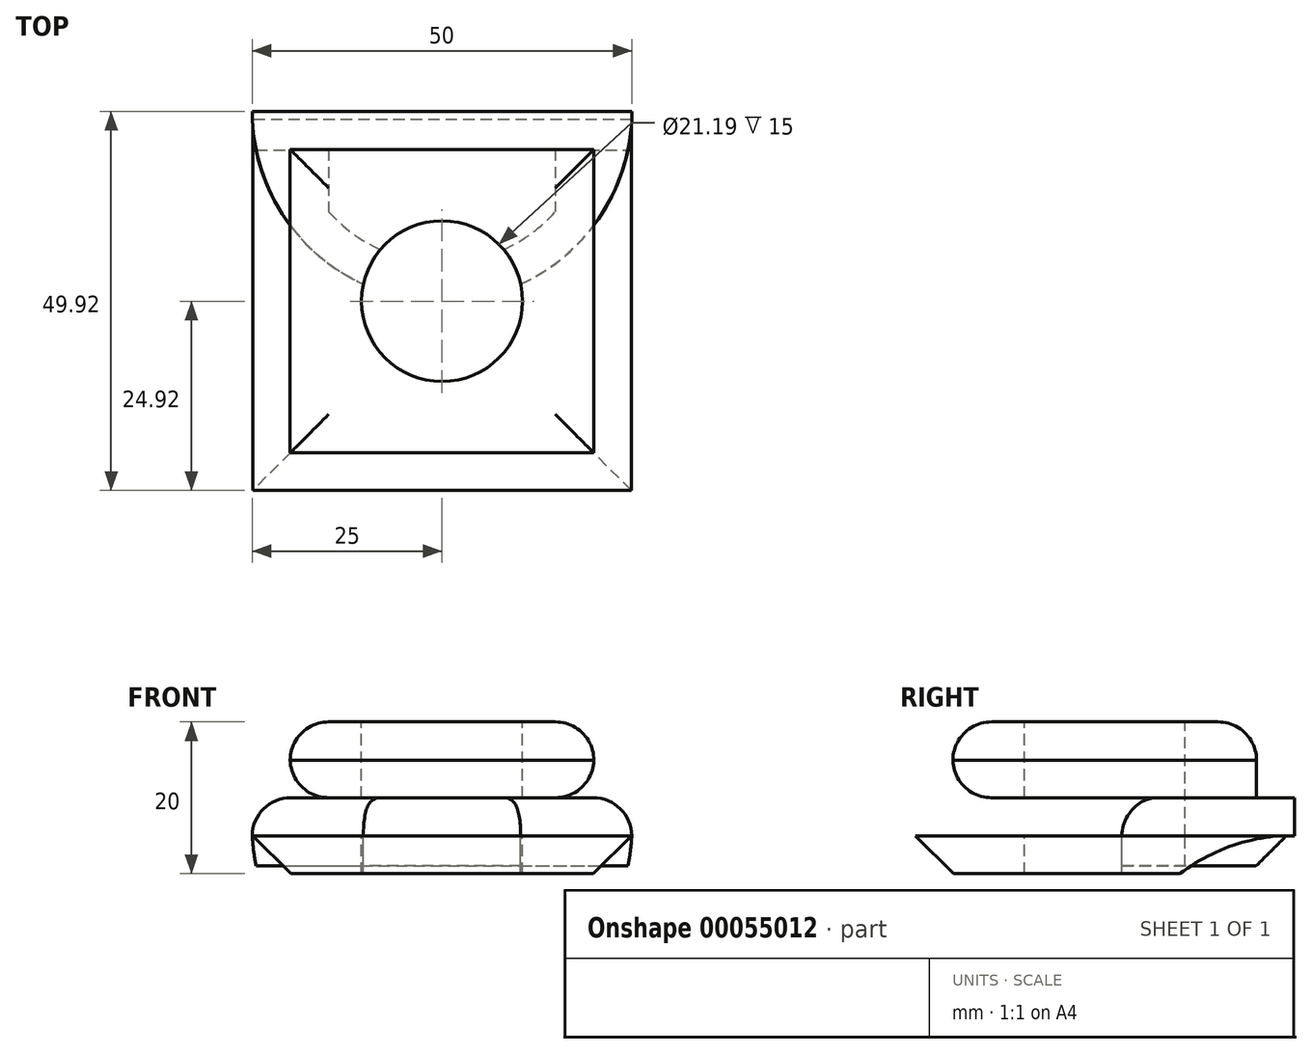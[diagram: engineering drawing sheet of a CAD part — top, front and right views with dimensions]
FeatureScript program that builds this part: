
annotation { "Feature Type Name" : "Feature", "Feature Type Description" : "" }
export const myFeature = defineFeature(function(context is Context, id is Id, definition is map)
    precondition{}
    {
        {
            var Q0;
            Q0=qCreatedBy(makeId("Top.planeOp"),FACE);
            var sketch = newSketch(context, id + "F0", { "sketchPlane" : qUnion([Q0])});
            skLineSegment(sketch, "E0.rect.bottom", {"start": v(25, -25) * mm, "end": v(-25, -25) * mm});
            skLineSegment(sketch, "E0.rect.top", {"start": v(25, 25) * mm, "end": v(-25, 25) * mm});
            skLineSegment(sketch, "E0.rect.left", {"start": v(25, -25) * mm, "end": v(25, 25) * mm});
            skLineSegment(sketch, "E0.rect.right", {"start": v(-25, -25) * mm, "end": v(-25, 25) * mm});
            skPoint(sketch, "E0.rect.middle", {"position": v(0, 0) * mm});
            skArc(sketch, "E1", {"start": v(-25, 25) * mm, "mid": v(0, 0) * mm, "end": v(25, 25) * mm});
            skSolve(sketch);
        }
        {
            var Q0;
            Q0=makeQuery(id+"F0.imprint","IMPRINT",FACE,{"disambiguationData":[TD([[makeQuery(id+"F0.imprint","IMPRINT",EDGE,{"derivedFrom":sQuery(id+"F0.wireOp",EDGE,"E0.rect.bottom")}),-1.0]])]});
            extrude(context, id + "F1", {"entities" : qUnion([Q0]), "oppositeDirection" : true, "depth" : 5 * mm});
        }
        {
            var Q0;
            Q0=makeQuery(id+"F0.imprint","IMPRINT",FACE,{"disambiguationData":[TD([[makeQuery(id+"F0.imprint","IMPRINT",EDGE,{"derivedFrom":sQuery(id+"F0.wireOp",EDGE,"E0.rect.top")}),1.0]])]});
            extrude(context, id + "F2", {"entities" : qUnion([Q0]), "operationType" : NewBodyOperationType.ADD, "depth" : 5 * mm});
        }
        {
            var Q0;
            Q0=makeQuery(id+"F2.opExtrude","CAP_EDGE",EDGE,{"disambiguationData":[OSD([sQuery(id+"F0.wireOp",EDGE,"E1")])],"isStart":false});
            fillet(context, id + "F3", {"entities" : qUnion([Q0]), "radius" : 5.08 * mm, "tangentPropagation" : true, "allowEdgeOverflow" : false});
        }
        {
            var Q0;
            Q0=makeQuery(id+"F2.opExtrude","CAP_FACE",FACE,{"disambiguationData":[OSD([sQuery(id+"F0.wireOp",EDGE,"E0.rect.top"),sQuery(id+"F0.wireOp",EDGE,"E1")])],"isStart":true});
            extrude(context, id + "F4", {"entities" : qUnion([Q0]), "depth" : 4 * mm});
        }
        {
            var Q0;
            Q0=makeQuery(id+"F1.opExtrude","CAP_EDGE",EDGE,{"disambiguationData":[OSD([sQuery(id+"F0.wireOp",EDGE,"E0.rect.right")])],"isStart":false});
            var Q1;
            Q1=makeQuery(id+"F1.opExtrude","CAP_EDGE",EDGE,{"disambiguationData":[OSD([sQuery(id+"F0.wireOp",EDGE,"E0.rect.bottom")])],"isStart":false});
            var Q2;
            Q2=makeQuery(id+"F1.opExtrude","CAP_EDGE",EDGE,{"disambiguationData":[OSD([sQuery(id+"F0.wireOp",EDGE,"E0.rect.left")])],"isStart":false});
            var Q3;
            Q3=makeQuery(id+"F4.opExtrude","CAP_EDGE",EDGE,{"disambiguationData":[OSD([sQuery(id+"F0.wireOp",EDGE,"E0.rect.top")])],"isStart":false});
            chamfer(context, id + "F5", {"entities" : qUnion([Q0, Q1, Q2, Q3]), "width" : 5.08 * mm, "tangentPropagation" : true});
        }
        {
            var Q0;
            Q0=makeQuery(id+"F2.opExtrude","CAP_FACE",FACE,{"disambiguationData":[OSD([sQuery(id+"F0.wireOp",EDGE,"E0.rect.top"),sQuery(id+"F0.wireOp",EDGE,"E1")])],"isStart":false});
            cPlane(context, id + "F6", {"entities" : qUnion([Q0]), "cplaneType" : CPlaneType.OFFSET, "offset" : 0 * mm, "width" : 152.4 * mm, "height" : 152.4 * mm});
        }
        {
            var Q0;
            Q0=qCreatedBy(id+"F6.planeOp",FACE);
            var sketch = newSketch(context, id + "F7", { "sketchPlane" : qUnion([Q0])});
            skLineSegment(sketch, "E2.rect.bottom", {"start": v(-20, 20) * mm, "end": v(20, 20) * mm});
            skLineSegment(sketch, "E2.rect.top", {"start": v(-20, -20) * mm, "end": v(20, -20) * mm});
            skLineSegment(sketch, "E2.rect.left", {"start": v(-20, 20) * mm, "end": v(-20, -20) * mm});
            skLineSegment(sketch, "E2.rect.right", {"start": v(20, 20) * mm, "end": v(20, -20) * mm});
            skPoint(sketch, "E2.rect.middle", {"position": v(0, 0) * mm});
            skSolve(sketch);
        }
        {
            var Q0;
            Q0 = qSketchRegion(id + "F7", true);
            extrude(context, id + "F8", {"entities" : qUnion([Q0]), "operationType" : NewBodyOperationType.ADD, "depth" : 10 * mm});
        }
        {
            var Q0;
            Q0=makeQuery(id+"F8.opExtrude","CAP_EDGE",EDGE,{"disambiguationData":[OSD([sQuery(id+"F7.wireOp",EDGE,"E2.rect.left")])],"isStart":false});
            var Q1;
            Q1=makeQuery(id+"F8.opExtrude","CAP_EDGE",EDGE,{"disambiguationData":[OSD([sQuery(id+"F7.wireOp",EDGE,"E2.rect.bottom")])],"isStart":false});
            var Q2;
            Q2=makeQuery(id+"F8.opExtrude","CAP_EDGE",EDGE,{"disambiguationData":[OSD([sQuery(id+"F7.wireOp",EDGE,"E2.rect.right")])],"isStart":false});
            var Q3;
            Q3=makeQuery(id+"F8.opExtrude","CAP_EDGE",EDGE,{"disambiguationData":[OSD([sQuery(id+"F7.wireOp",EDGE,"E2.rect.top")])],"isStart":false});
            fillet(context, id + "F9", {"entities" : qUnion([Q0, Q1, Q2, Q3]), "radius" : 5.08 * mm, "tangentPropagation" : true, "allowEdgeOverflow" : false});
        }
        {
            var Q0;
            Q0=makeQuery(id+"F8.opExtrude","CAP_EDGE",EDGE,{"disambiguationData":[OSD([sQuery(id+"F7.wireOp",EDGE,"E2.rect.right")])],"isStart":true});
            var Q1;
            Q1=makeQuery(id+"F8.opExtrude","CAP_EDGE",EDGE,{"disambiguationData":[OSD([sQuery(id+"F7.wireOp",EDGE,"E2.rect.top")])],"isStart":true});
            var Q2;
            Q2=makeQuery(id+"F8.opExtrude","CAP_EDGE",EDGE,{"disambiguationData":[OSD([sQuery(id+"F7.wireOp",EDGE,"E2.rect.left")])],"isStart":true});
            fillet(context, id + "F10", {"entities" : qUnion([Q0, Q1, Q2]), "radius" : 5.08 * mm, "tangentPropagation" : true, "allowEdgeOverflow" : false});
        }
        {
            var Q0;
            Q0=makeQuery(id+"F8.opExtrude","CAP_FACE",FACE,{"disambiguationData":[OSD([sQuery(id+"F7.wireOp",EDGE,"E2.rect.bottom"),sQuery(id+"F7.wireOp",EDGE,"E2.rect.top"),sQuery(id+"F7.wireOp",EDGE,"E2.rect.left"),sQuery(id+"F7.wireOp",EDGE,"E2.rect.right")])],"isStart":false});
            cPlane(context, id + "F11", {"entities" : qUnion([Q0]), "cplaneType" : CPlaneType.OFFSET, "offset" : 0 * mm, "width" : 152.4 * mm, "height" : 152.4 * mm});
        }
        {
            var Q0;
            Q0=qCreatedBy(id+"F11.planeOp",FACE);
            var sketch = newSketch(context, id + "F12", { "sketchPlane" : qUnion([Q0])});
            skCircle(sketch, "E3", {"center": v(0, 0) * mm, "radius": 10.6 * mm});
            skSolve(sketch);
        }
        {
            var Q0;
            Q0 = qSketchRegion(id + "F12", true);
            extrude(context, id + "F13", {"entities" : qUnion([Q0]), "operationType" : NewBodyOperationType.REMOVE, "oppositeDirection" : true, "depth" : 76.2 * mm});
        }
    });
